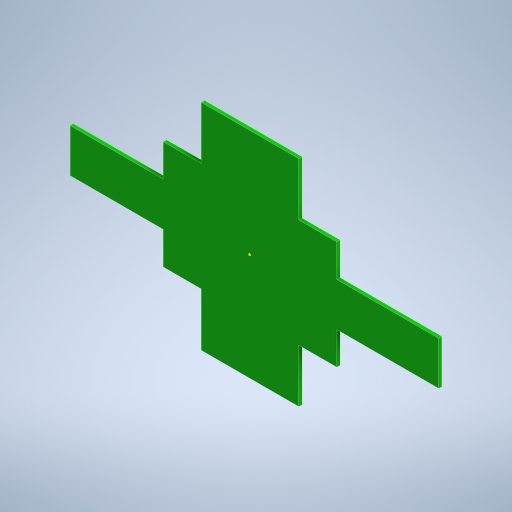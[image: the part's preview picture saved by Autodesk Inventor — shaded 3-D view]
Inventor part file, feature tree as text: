
AUTODESK INVENTOR PART (.ipt)
format: ipt  version: 2024 (Build 280153000, 153)  size: 248,832 bytes
history: native  units: mm
features: sketch x2, extrude x1
ambient origin geometry x8: Origin, YZ Plane, XZ Plane, XY Plane, X Axis, Y Axis, Z Axis, Center Point
bodies: Volumenkörper1 (feature_tree)
feature tree (3):
  sketch  "Skizze1"  dims[d0=340.0mm d1=40.0mm]
  extrude  "Extrusion1"  Depth=40.0mm
  sketch  "Skizze2"  dims[d2=100.0mm d3=198.0mm d4=160.0mm d5=90.0mm d6=86.025249mm d7=3.0mm d8=0.0mm]
